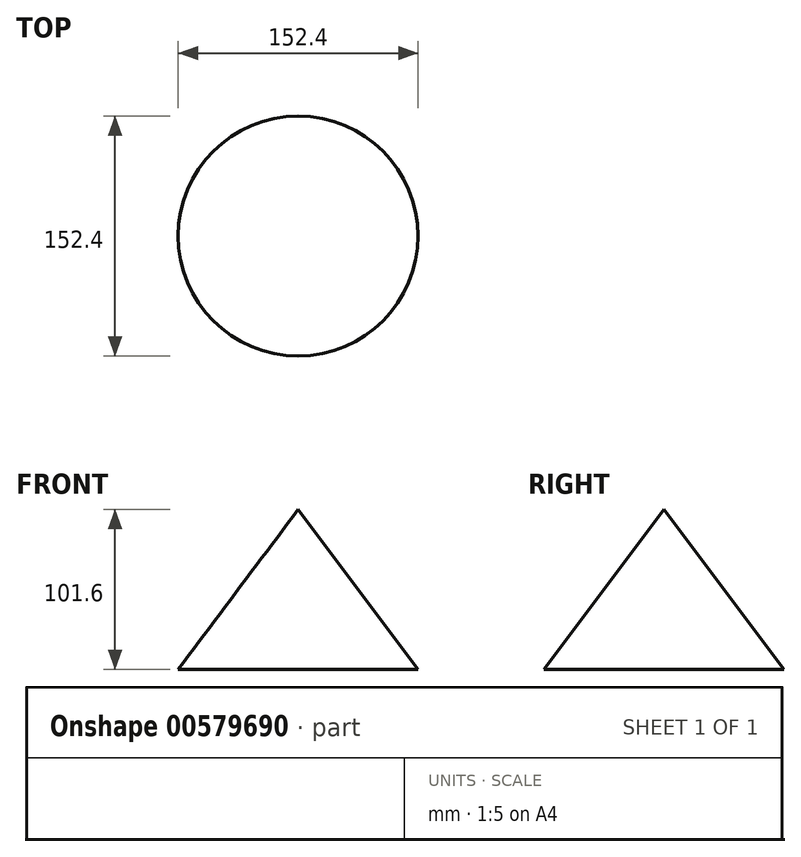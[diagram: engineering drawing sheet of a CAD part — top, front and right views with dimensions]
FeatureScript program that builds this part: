
annotation { "Feature Type Name" : "Feature", "Feature Type Description" : "" }
export const myFeature = defineFeature(function(context is Context, id is Id, definition is map)
    precondition{}
    {
        {
            var Q0;
            Q0=qCreatedBy(makeId("Front.planeOp"),FACE);
            var sketch = newSketch(context, id + "F0", { "sketchPlane" : qUnion([Q0])});
            skLineSegment(sketch, "E0", {"start": v(0, 0) * mm, "end": v(76.2, 0) * mm});
            skLineSegment(sketch, "E1", {"start": v(0, 0) * mm, "end": v(0, 101.6) * mm});
            skLineSegment(sketch, "E2", {"start": v(0, 101.6) * mm, "end": v(76.2, 0) * mm});
            skSolve(sketch);
        }
        {
            var Q0;
            Q0=makeQuery(id+"F0.imprint","IMPRINT",FACE,{"disambiguationData":[TD([[makeQuery(id+"F0.imprint","IMPRINT",EDGE,{"derivedFrom":sQuery(id+"F0.wireOp",EDGE,"E0")}),1.0]])]});
            var Q1;
            Q1=sQuery(id+"F0.wireOp",EDGE,"E1");
            revolve(context, id + "F1", {"entities" : qUnion([Q0]), "axis" : qUnion([Q1]), "revolveType" : RevolveType.FULL});
        }
    });
